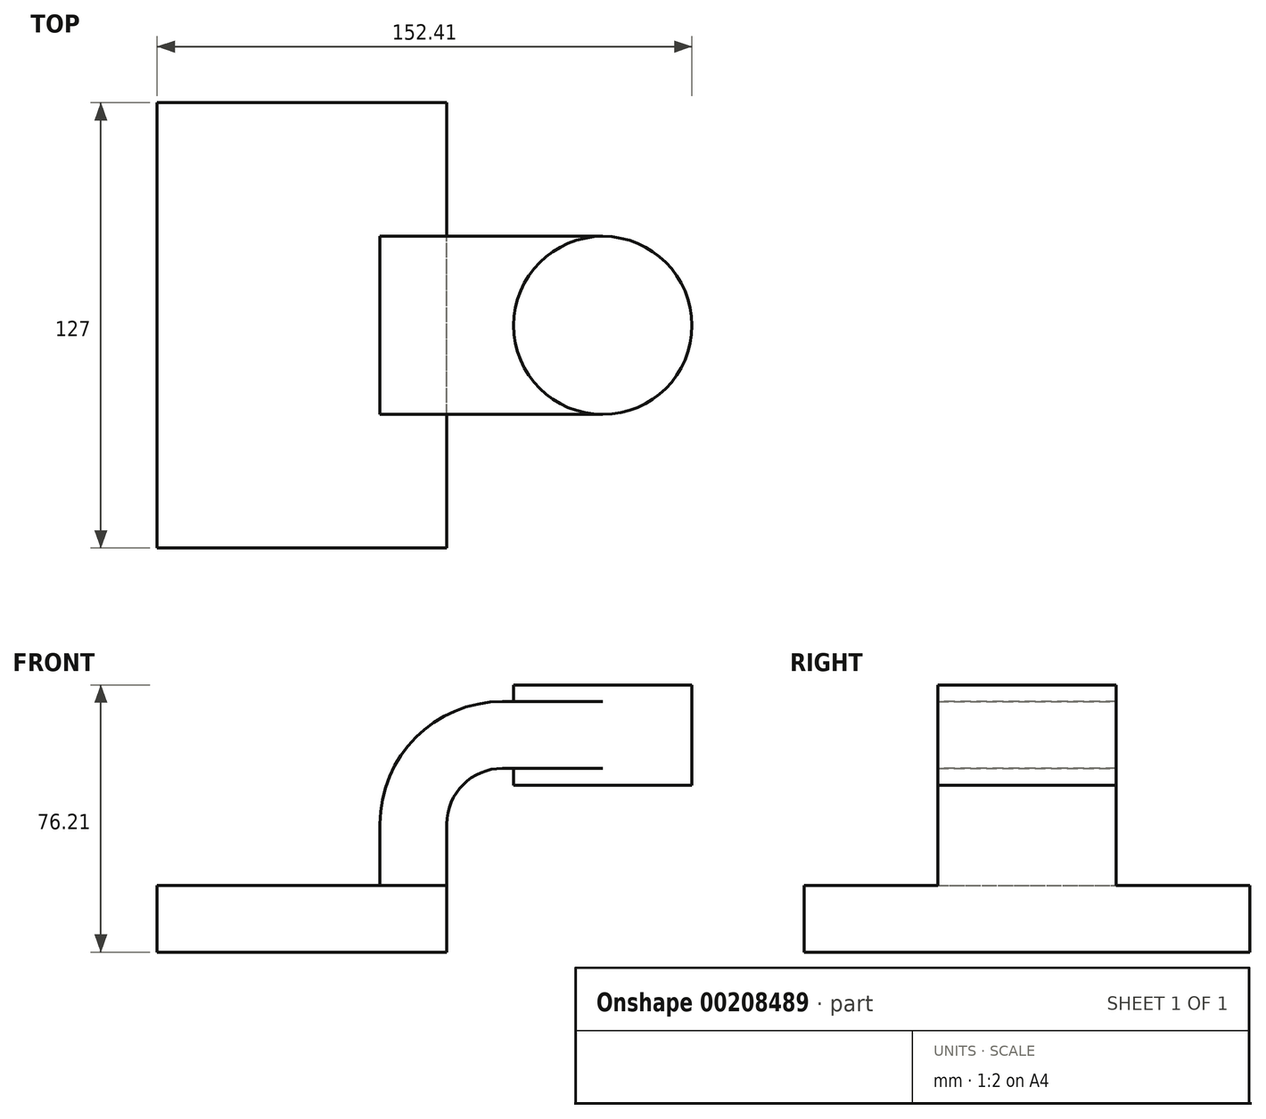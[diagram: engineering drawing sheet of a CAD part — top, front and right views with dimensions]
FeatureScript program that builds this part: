
annotation { "Feature Type Name" : "Feature", "Feature Type Description" : "" }
export const myFeature = defineFeature(function(context is Context, id is Id, definition is map)
    precondition{}
    {
        {
            var Q0;
            Q0=qCreatedBy(makeId("Front.planeOp"),FACE);
            var sketch = newSketch(context, id + "F0", { "sketchPlane" : qUnion([Q0])});
            skLineSegment(sketch, "E0.bottom", {"start": v(41.27, 9.53) * mm, "end": v(-41.28, 9.53) * mm});
            skLineSegment(sketch, "E0.top", {"start": v(41.28, -9.52) * mm, "end": v(-41.27, -9.52) * mm});
            skLineSegment(sketch, "E0.left", {"start": v(41.28, 9.53) * mm, "end": v(41.28, -9.52) * mm});
            skLineSegment(sketch, "E0.right", {"start": v(-41.28, 9.53) * mm, "end": v(-41.27, -9.52) * mm});
            skPoint(sketch, "E0.middle", {"position": v(0, 0) * mm});
            skLineSegment(sketch, "E1.bottom", {"start": v(111.12, 66.68) * mm, "end": v(60.32, 66.68) * mm});
            skLineSegment(sketch, "E1.top", {"start": v(111.12, 38.1) * mm, "end": v(60.32, 38.1) * mm});
            skLineSegment(sketch, "E1.left", {"start": v(111.12, 66.68) * mm, "end": v(111.12, 38.1) * mm});
            skLineSegment(sketch, "E1.right", {"start": v(60.32, 66.68) * mm, "end": v(60.32, 38.1) * mm});
            skPoint(sketch, "E1.middle", {"position": v(85.72, 52.39) * mm});
            skLineSegment(sketch, "E2", {"start": v(41.27, 9.53) * mm, "end": v(41.27, 27) * mm});
            skArc(sketch, "E3", {"start": v(41.27, 27) * mm, "mid": v(45.92, 38.23) * mm, "end": v(57.15, 42.88) * mm});
            skLineSegment(sketch, "E4", {"start": v(57.15, 42.88) * mm, "end": v(85.72, 42.88) * mm});
            skLineSegment(sketch, "E5.0", {"start": v(57.15, 61.93) * mm, "end": v(85.72, 61.93) * mm});
            skArc(sketch, "E5.1", {"start": v(22.22, 27) * mm, "mid": v(32.45, 51.7) * mm, "end": v(57.15, 61.93) * mm});
            skLineSegment(sketch, "E5.2", {"start": v(22.22, 9.53) * mm, "end": v(22.22, 27) * mm});
            skFitSpline(sketch, "E6", {"points": [v(-41.28, 9.52) * mm, v(57.15, 61.93) * mm], "startDerivative": vector(28.82, 70.52) * mm, "endDerivative": vector(125.72, -6.25) * mm});
            skLineSegment(sketch, "E7", {"start": v(85.72, 66.68) * mm, "end": v(85.72, 38.1) * mm});
            skSolve(sketch);
        }
        {
            var Q0;
            Q0=makeQuery(id+"F0.imprint","IMPRINT",FACE,{"disambiguationData":[TD([[makeQuery(id+"F0.imprint","IMPRINT",EDGE,{"derivedFrom":sQuery(id+"F0.wireOp",EDGE,"E0.top")}),-1.0]])]});
            extrude(context, id + "F1", {"entities" : qUnion([Q0]), "endBound" : BoundingType.SYMMETRIC, "depth" : 127 * mm});
        }
        {
            var Q0;
            {var subQ1=sQuery(id+"F0.wireOp",EDGE,"E2");Q0=makeQuery(id+"F0.imprint","IMPRINT",FACE,{"disambiguationData":[TD([[makeQuery(id+"F0.imprint","IMPRINT",EDGE,{"derivedFrom":subQ1}),1.0]])]});}
            var Q1;
            {var subQ0=sQuery(id+"F0.wireOp",EDGE,"E5.0");var subQ1=sQuery(id+"F0.wireOp",EDGE,"E1.right");var subQ2=makeQuery(id+"F0.imprint","INTERSECT",VERTEX,{"derivedFrom":[subQ1,subQ0]});Q1=makeQuery(id+"F0.imprint","IMPRINT",FACE,{"disambiguationData":[TD([[makeQuery(id+"F0.imprint","IMPRINT",EDGE,{"disambiguationData":[TD([[subQ2,-1.0]])],"derivedFrom":subQ1}),1.0]])]});}
            extrude(context, id + "F2", {"entities" : qUnion([Q0, Q1]), "operationType" : NewBodyOperationType.ADD, "endBound" : BoundingType.SYMMETRIC, "depth" : 50.8 * mm});
        }
        {
            var Q0;
            Q0=makeQuery(id+"F0.imprint","IMPRINT",FACE,{"disambiguationData":[TD([[makeQuery(id+"F0.imprint","IMPRINT",EDGE,{"derivedFrom":sQuery(id+"F0.wireOp",EDGE,"E5.1")}),1.0]])]});
            extrude(context, id + "F3", {"entities" : qUnion([Q0]), "operationType" : NewBodyOperationType.ADD, "endBound" : BoundingType.SYMMETRIC, "depth" : 15.88 * mm});
        }
        {
            var Q0;
            {var subQ0=sQuery(id+"F0.wireOp",EDGE,"E1.left");Q0=makeQuery(id+"F0.imprint","IMPRINT",FACE,{"disambiguationData":[TD([[makeQuery(id+"F0.imprint","IMPRINT",EDGE,{"derivedFrom":subQ0}),-1.0]])]});}
            var Q1;
            Q1=sQuery(id+"F0.wireOp",EDGE,"E7");
            revolve(context, id + "F4", {"operationType" : NewBodyOperationType.ADD, "entities" : qUnion([Q0]), "axis" : qUnion([Q1]), "revolveType" : RevolveType.FULL});
        }
    });
